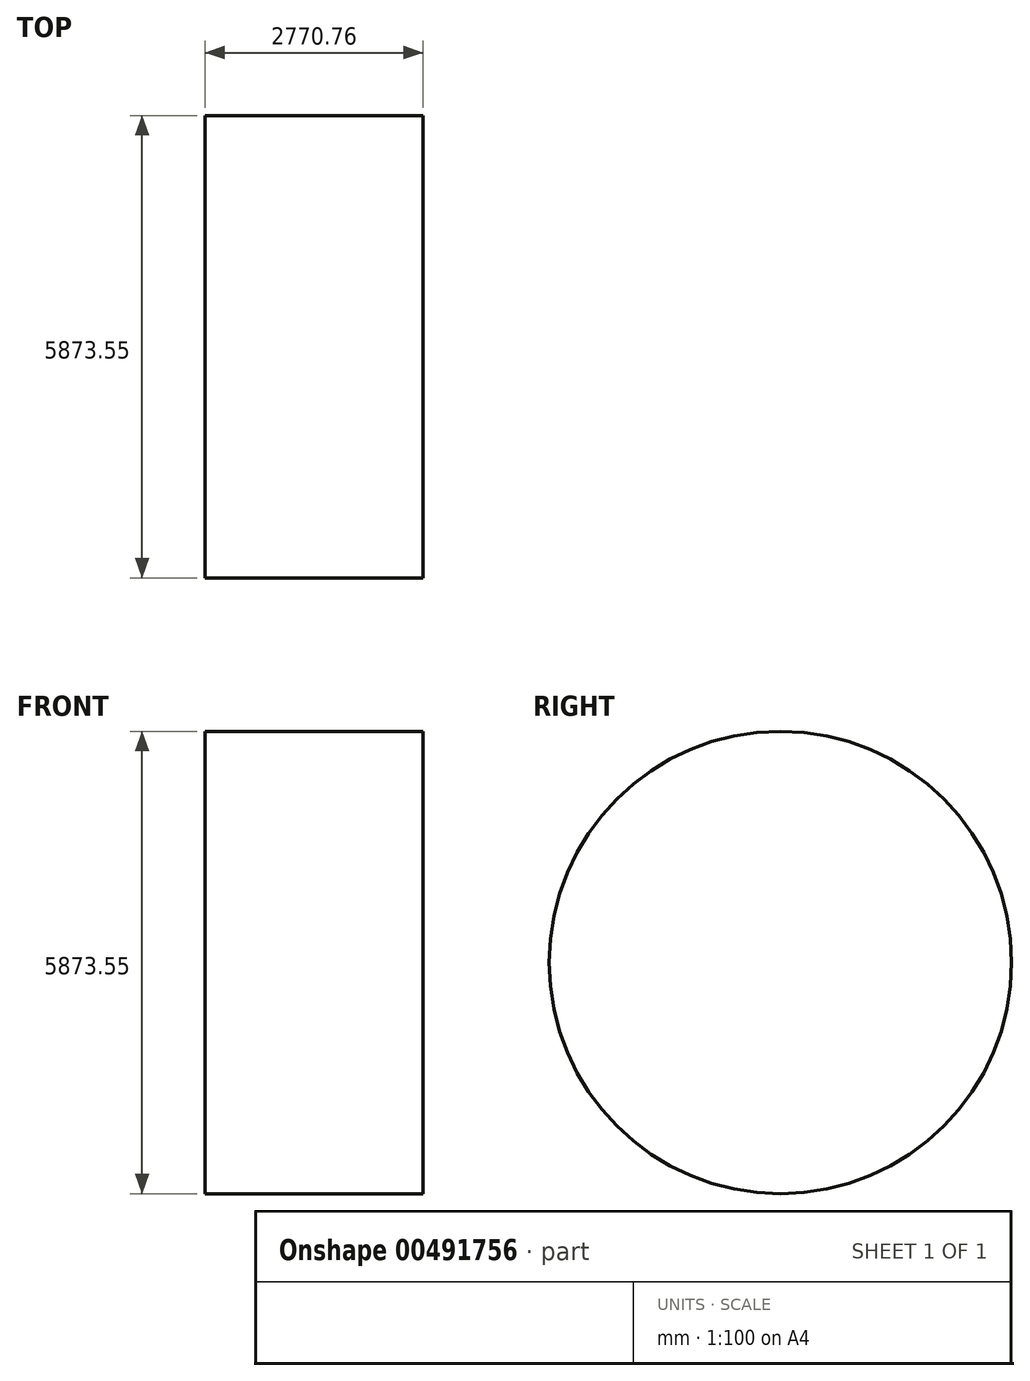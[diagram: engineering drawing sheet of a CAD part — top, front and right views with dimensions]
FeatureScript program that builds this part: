
annotation { "Feature Type Name" : "Feature", "Feature Type Description" : "" }
export const myFeature = defineFeature(function(context is Context, id is Id, definition is map)
    precondition{}
    {
        {
            var Q0;
            Q0=qCreatedBy(makeId("Right.planeOp"),FACE);
            var sketch = newSketch(context, id + "F0", { "sketchPlane" : qUnion([Q0])});
            skCircle(sketch, "E0", {"center": v(-326.45, 173.2) * mm, "radius": 197.39 * mm});
            skCircle(sketch, "E1", {"center": v(562.55, -255.78) * mm, "radius": 2936.78 * mm});
            skSolve(sketch);
        }
        {
            var Q0;
            Q0=makeQuery(id+"F0.imprint","IMPRINT",FACE,{"disambiguationData":[TD([[makeQuery(id+"F0.imprint","IMPRINT",EDGE,{"derivedFrom":sQuery(id+"F0.wireOp",EDGE,"E0")}),1.0]])]});
            var Q1;
            Q1=makeQuery(id+"F0.imprint","IMPRINT",FACE,{"disambiguationData":[TD([[makeQuery(id+"F0.imprint","IMPRINT",EDGE,{"derivedFrom":sQuery(id+"F0.wireOp",EDGE,"E0")}),-1.0]])]});
            extrude(context, id + "F1", {"entities" : qUnion([Q0, Q1]), "depth" : 2770.76 * mm});
        }
    });
